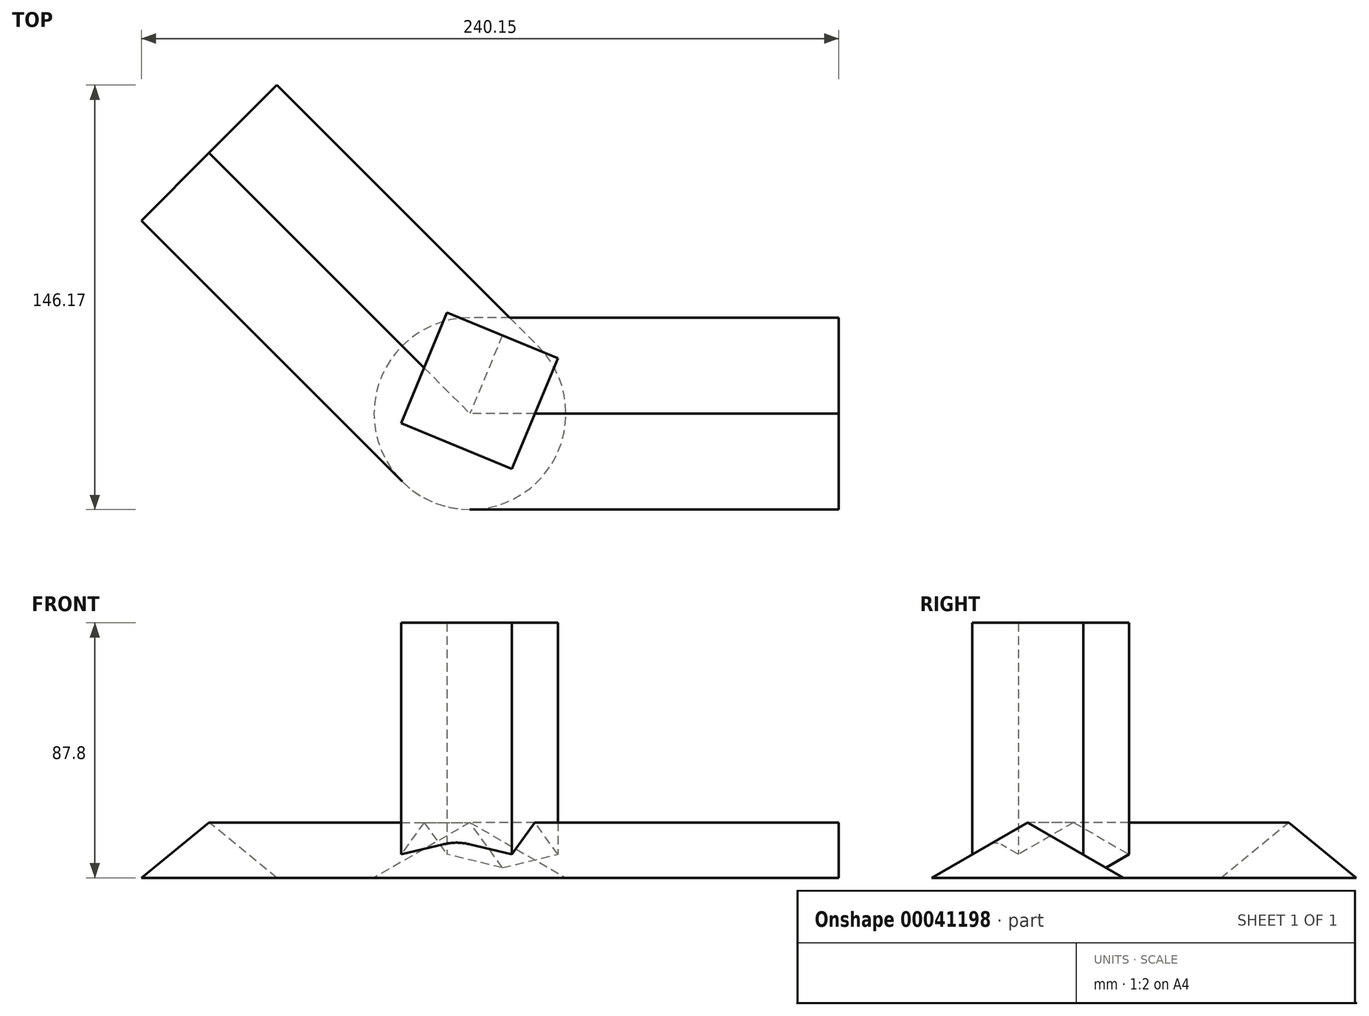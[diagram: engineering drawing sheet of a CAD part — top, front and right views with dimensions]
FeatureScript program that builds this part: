
annotation { "Feature Type Name" : "Feature", "Feature Type Description" : "" }
export const myFeature = defineFeature(function(context is Context, id is Id, definition is map)
    precondition{}
    {
        {
            var Q0;
            Q0=qCreatedBy(makeId("Right.planeOp"),FACE);
            var sketch = newSketch(context, id + "F0", { "sketchPlane" : qUnion([Q0])});
            skLineSegment(sketch, "E0", {"start": v(0, 0) * mm, "end": v(33.02, 0) * mm});
            skLineSegment(sketch, "E1", {"start": v(33.02, 0) * mm, "end": v(0, 19.06) * mm});
            skLineSegment(sketch, "E2", {"start": v(0, 19.06) * mm, "end": v(0, 0) * mm});
            skLineSegment(sketch, "E3", {"start": v(0, 32.53) * mm, "end": v(0, 60.6) * mm, "construction": true});
            skSolve(sketch);
        }
        {
            var Q0;
            Q0 = qSketchRegion(id + "F0", true);
            var Q1;
            Q1=sQuery(id+"F0.wireOp",EDGE,"E3");
            revolve(context, id + "F1", {"entities" : qUnion([Q0]), "axis" : qUnion([Q1]), "revolveType" : RevolveType.ONE_DIRECTION, "angle" : 180 * degree});
        }
        {
            var Q0;
            Q0=makeQuery(id+"F1.opRevolve","CAP_FACE",FACE,{"disambiguationData":[OSD([sQuery(id+"F0.wireOp",EDGE,"E0"),sQuery(id+"F0.wireOp",EDGE,"E1"),sQuery(id+"F0.wireOp",EDGE,"E2")])],"isStart":false});
            extrude(context, id + "F2", {"entities" : qUnion([Q0]), "operationType" : NewBodyOperationType.ADD, "depth" : 127 * mm});
        }
        {
            var Q0;
            Q0=makeQuery(id+"F1.opRevolve","SWEPT_BODY",BODY,{"disambiguationData":[OSD([sQuery(id+"F0.wireOp",EDGE,"E0"),sQuery(id+"F0.wireOp",EDGE,"E1"),sQuery(id+"F0.wireOp",EDGE,"E2")])]});
            var Q1;
            Q1=sQuery(id+"F0.wireOp",EDGE,"E3");
            transform(context, id + "F3", {"entities" : qUnion([Q0]), "transformType" : TransformType.ROTATION, "transformAxis" : qUnion([Q1]), "angle" : 135 * degree, "makeCopy" : true});
        }
        {
            var Q0;
            Q0=qCreatedBy(makeId("Top.planeOp"),FACE);
            var sketch = newSketch(context, id + "F4", { "sketchPlane" : qUnion([Q0])});
            skPoint(sketch, "E4.rect.middle", {"position": v(0, 0) * mm});
            skLineSegment(sketch, "E5.rect.bottom", {"start": v(14.44, -19.07) * mm, "end": v(-23.7, -3.27) * mm});
            skLineSegment(sketch, "E5.rect.top", {"start": v(30.24, 19.07) * mm, "end": v(-7.9, 34.86) * mm});
            skLineSegment(sketch, "E5.rect.left", {"start": v(14.44, -19.07) * mm, "end": v(30.24, 19.07) * mm});
            skLineSegment(sketch, "E5.rect.right", {"start": v(-23.7, -3.27) * mm, "end": v(-7.9, 34.86) * mm});
            skLineSegment(sketch, "E6", {"start": v(22.34, 0) * mm, "end": v(-15.8, 15.8) * mm, "construction": true});
            skSolve(sketch);
        }
        {
            var Q0;
            Q0 = qSketchRegion(id + "F4", true);
            extrude(context, id + "F5", {"entities" : qUnion([Q0]), "depth" : 87.8 * mm});
        }
        {
            var Q0;
            Q0=makeQuery(id+"F1.opRevolve","SWEPT_BODY",BODY,{"disambiguationData":[OSD([sQuery(id+"F0.wireOp",EDGE,"E0"),sQuery(id+"F0.wireOp",EDGE,"E1"),sQuery(id+"F0.wireOp",EDGE,"E2")])]});
            var Q1;
            Q1=makeQuery(id+"F3.opPattern","COPY",BODY,{"derivedFrom":makeQuery(id+"F1.opRevolve","SWEPT_BODY",BODY,{"disambiguationData":[OSD([sQuery(id+"F0.wireOp",EDGE,"E0"),sQuery(id+"F0.wireOp",EDGE,"E1"),sQuery(id+"F0.wireOp",EDGE,"E2")])]}),"instanceName":"1"});
            var Q2;
            Q2=makeQuery(id+"F5.opExtrude","SWEPT_BODY",BODY,{"disambiguationData":[OSD([sQuery(id+"F4.wireOp",EDGE,"E5.rect.bottom"),sQuery(id+"F4.wireOp",EDGE,"E5.rect.top"),sQuery(id+"F4.wireOp",EDGE,"E5.rect.left"),sQuery(id+"F4.wireOp",EDGE,"E5.rect.right")])]});
            booleanBodies(context, id + "F6", {"operationType" : BooleanOperationType.SUBTRACTION, "tools" : qUnion([Q0, Q1]), "targets" : qUnion([Q2]), "keepTools" : true});
        }
    });
